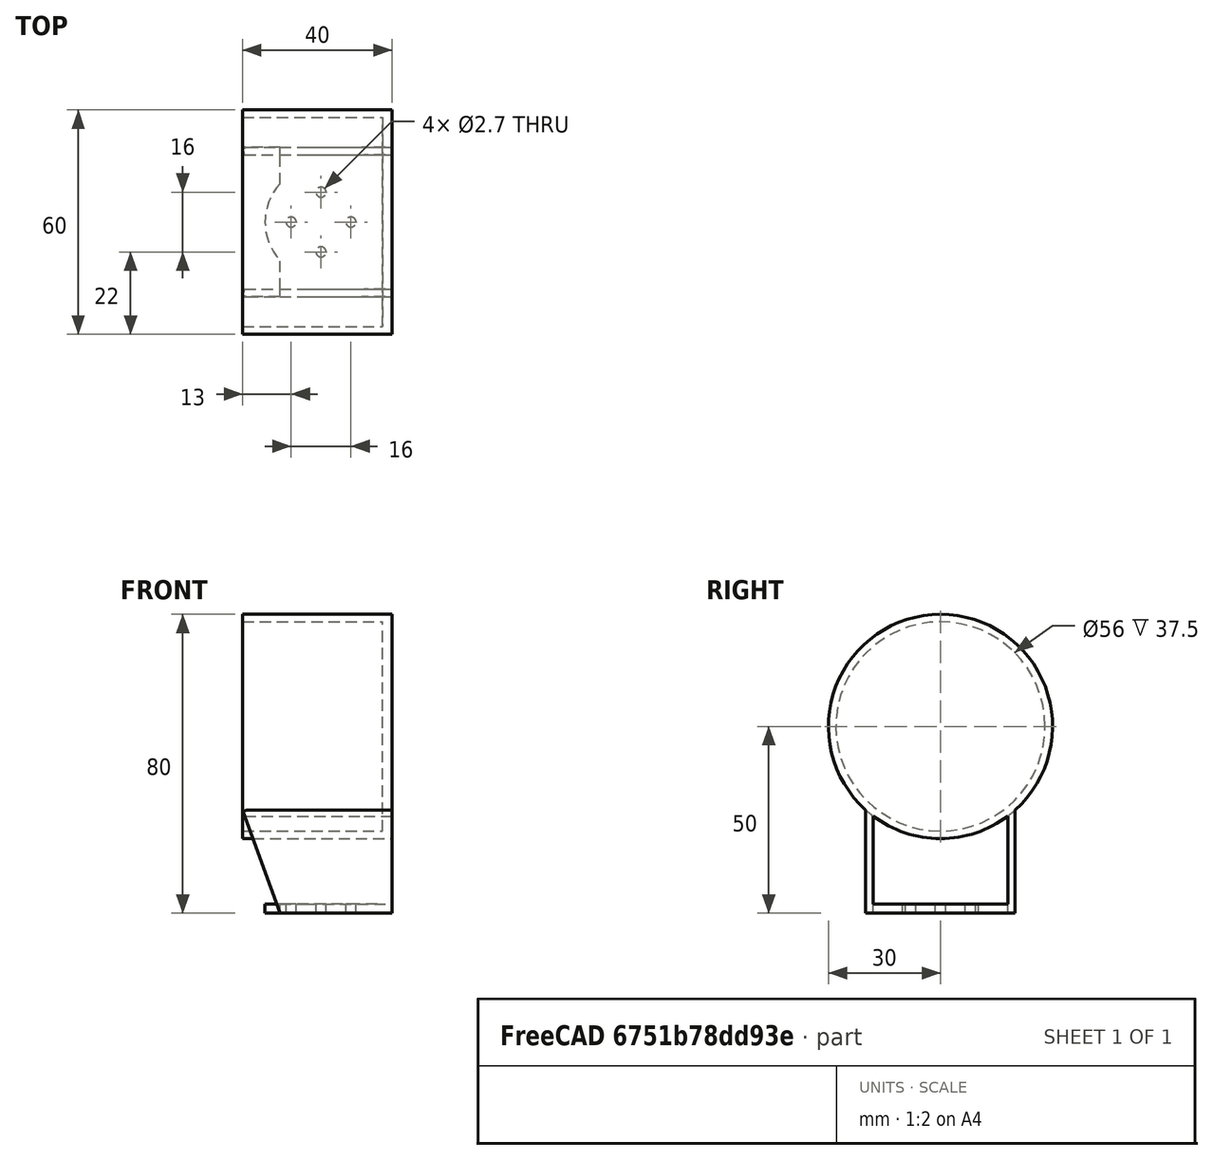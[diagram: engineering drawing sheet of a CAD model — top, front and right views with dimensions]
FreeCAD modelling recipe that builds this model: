
FCSTD DOCUMENT  (FreeCAD 0.15R4671 (Git))
Label: cup
License: All rights reserved
LicenseURL: http://en.wikipedia.org/wiki/All_rights_reserved
objects: Part::Cylinder×7, Part::Box×5, Part::MultiFuse×3, Part::Cut×1
note: 16 computed .brp shape members not serialized (recipe doc carries the construction recipe); baked Part::Feature solids carry a one-line shape summary decoded from their .brp

FEATURE [Part::Cylinder] Cylinder
  Angle = 360
  Height = 10
  Placement = pos=(0,-8,-3) rot=(0,0,1;0rad)
  Radius = 1.35
FEATURE [Part::Cylinder] Cylinder001
  Angle = 360
  Height = 10
  Placement = pos=(-8,0,-3) rot=(0,0,1;0rad)
  Radius = 1.35
FEATURE [Part::Cylinder] Cylinder002
  Angle = 360
  Height = 10
  Placement = pos=(8,0,-3) rot=(0,0,1;0rad)
  Radius = 1.35
FEATURE [Part::Cylinder] Cylinder003
  Angle = 360
  Height = 10
  Placement = pos=(0,8,-3) rot=(0,0,1;0rad)
  Radius = 1.35
FEATURE [Part::Box] Box  label="Cube"
  Height = 29
  Length = 30
  Placement = pos=(-11,18,0) rot=(0,-1,0;0.349066rad)
  Width = 2
FEATURE [Part::Cylinder] Cylinder004
  Angle = 360
  Height = 2.5
  Radius = 15
FEATURE [Part::Box] Box001  label="Cube001"
  Height = 2.5
  Length = 30
  Placement = pos=(-11,-20,0) rot=(0,0,1;0rad)
  Width = 40
FEATURE [Part::MultiFuse] Fusion
  Placement = pos=(0,0,-2) rot=(0,0,1;0rad)
  Shapes = -> [Cylinder,Cylinder001,Cylinder002,Cylinder003]
FEATURE [Part::Box] Box002  label="Cube002"
  Height = 40
  Length = 30
  Placement = pos=(-11,-20,0) rot=(0,0,1;0rad)
  Width = 2
FEATURE [Part::Cylinder] Cylinder005
  Angle = 360
  Height = 40
  Placement = pos=(-21,0,50) rot=(0,1,0;1.5708rad)
  Radius = 30
FEATURE [Part::Cylinder] Cylinder006
  Angle = 360
  Height = 37.5
  Placement = pos=(-21,0,50) rot=(0,1,0;1.5708rad)
  Radius = 28
FEATURE [Part::MultiFuse] Fusion002
  Shapes = -> [Cylinder006,Fusion]
FEATURE [Part::Box] Box003  label="Cube003"
  Height = 40
  Length = 30
  Placement = pos=(-11,18,0) rot=(0,0,1;0rad)
  Width = 2
FEATURE [Part::Box] Box004  label="Cube004"
  Height = 29
  Length = 30
  Placement = pos=(-11,-20,0) rot=(0,-1,0;0.349066rad)
  Width = 2
FEATURE [Part::MultiFuse] Fusion003
  Shapes = -> [Box004,Box,Box003,Cylinder005,Box002,Box001,Cylinder004]
FEATURE [Part::Cut] Cut
  Base = -> Fusion003
  Tool = -> Fusion002
